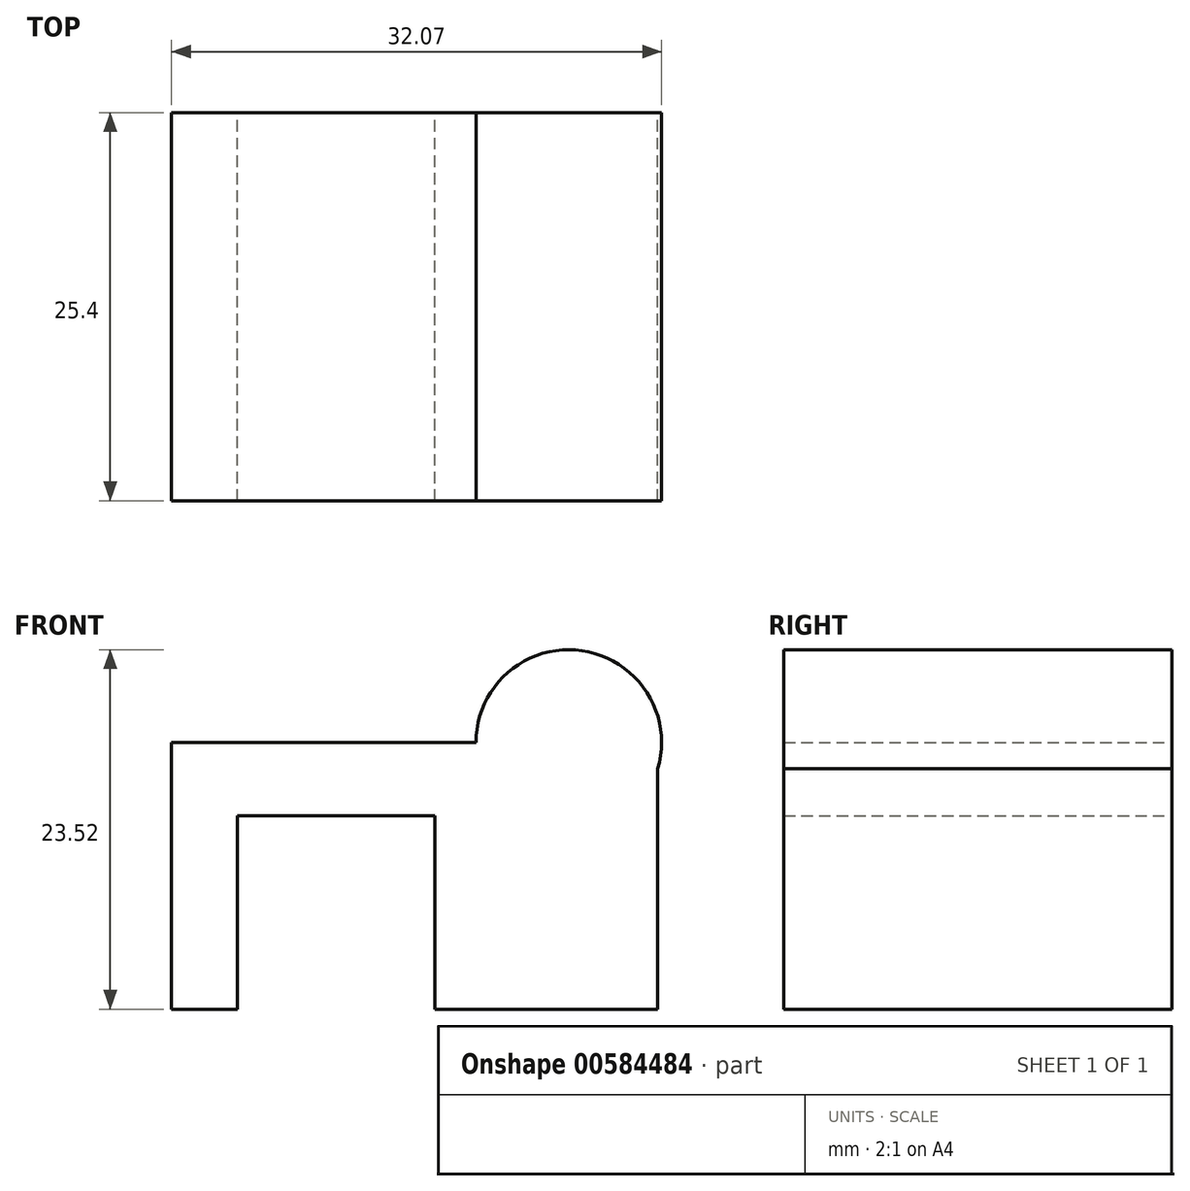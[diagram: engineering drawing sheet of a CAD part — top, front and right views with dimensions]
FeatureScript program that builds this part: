
annotation { "Feature Type Name" : "Feature", "Feature Type Description" : "" }
export const myFeature = defineFeature(function(context is Context, id is Id, definition is map)
    precondition{}
    {
        {
            var Q0;
            Q0=qCreatedBy(makeId("Front.planeOp"),FACE);
            var sketch = newSketch(context, id + "F0", { "sketchPlane" : qUnion([Q0])});
            skLineSegment(sketch, "E0.bottom", {"start": v(-53.54, 56.16) * mm, "end": v(-21.72, 56.16) * mm});
            skLineSegment(sketch, "E0.top", {"start": v(-53.54, 38.72) * mm, "end": v(-21.72, 38.72) * mm});
            skLineSegment(sketch, "E0.left", {"start": v(-53.54, 56.16) * mm, "end": v(-53.54, 38.72) * mm});
            skLineSegment(sketch, "E0.right", {"start": v(-21.72, 56.16) * mm, "end": v(-21.72, 38.72) * mm});
            skCircle(sketch, "E1", {"center": v(-27.55, 56.16) * mm, "radius": 6.07 * mm});
            skSolve(sketch);
        }
        {
            var Q0;
            Q0 = qSketchRegion(id + "F0", true);
            extrude(context, id + "F1", {"entities" : qUnion([Q0]), "depth" : 25.4 * mm, "offsetDistance" : 25.4 * mm});
        }
        {
            var Q0;
            Q0=qCreatedBy(makeId("Front.planeOp"),FACE);
            var sketch = newSketch(context, id + "F2", { "sketchPlane" : qUnion([Q0])});
            skLineSegment(sketch, "E2.bottom", {"start": v(-49.22, 51.38) * mm, "end": v(-36.32, 51.38) * mm});
            skLineSegment(sketch, "E2.top", {"start": v(-49.22, 26.3) * mm, "end": v(-36.32, 26.3) * mm});
            skLineSegment(sketch, "E2.left", {"start": v(-49.22, 51.38) * mm, "end": v(-49.22, 26.3) * mm});
            skLineSegment(sketch, "E2.right", {"start": v(-36.32, 51.38) * mm, "end": v(-36.32, 26.3) * mm});
            skArc(sketch, "E3", {"start": v(-32.75, 33.95) * mm, "mid": v(-19.07, 39.81) * mm, "end": v(-30.77, 49) * mm});
            skSolve(sketch);
        }
        {
            var Q0;
            Q0=makeQuery(id+"F2.imprint","IMPRINT",FACE,{"disambiguationData":[TD([[makeQuery(id+"F2.imprint","IMPRINT",EDGE,{"derivedFrom":sQuery(id+"F2.wireOp",EDGE,"E2.bottom")}),-1.0]])]});
            extrude(context, id + "F3", {"entities" : qUnion([Q0]), "operationType" : NewBodyOperationType.REMOVE, "depth" : 28.7 * mm, "offsetDistance" : 25.4 * mm});
        }
    });
